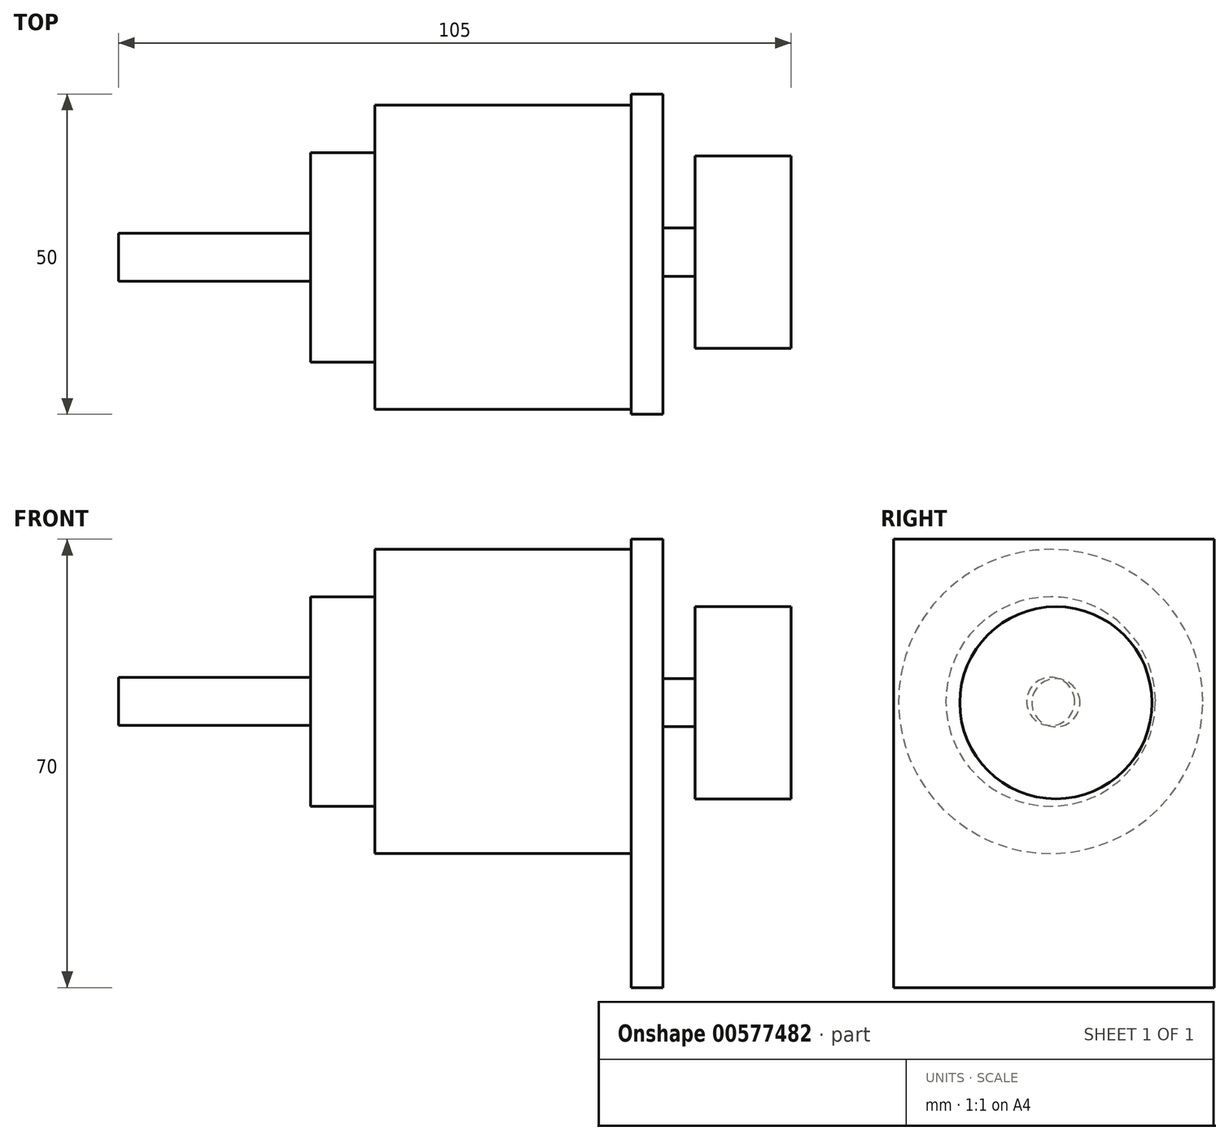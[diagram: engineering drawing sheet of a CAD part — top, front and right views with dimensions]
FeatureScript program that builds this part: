
annotation { "Feature Type Name" : "Feature", "Feature Type Description" : "" }
export const myFeature = defineFeature(function(context is Context, id is Id, definition is map)
    precondition{}
    {
        {
            var Q0;
            Q0=qCreatedBy(makeId("Front.planeOp"),FACE);
            var sketch = newSketch(context, id + "F0", { "sketchPlane" : qUnion([Q0])});
            skLineSegment(sketch, "E0.bottom", {"start": v(-2.5, 0.57) * mm, "end": v(2.5, 0.57) * mm});
            skLineSegment(sketch, "E0.top", {"start": v(-2.5, 70.57) * mm, "end": v(2.5, 70.57) * mm});
            skLineSegment(sketch, "E0.left", {"start": v(-2.5, 0.57) * mm, "end": v(-2.5, 70.57) * mm});
            skLineSegment(sketch, "E0.right", {"start": v(2.5, 0.57) * mm, "end": v(2.5, 70.57) * mm});
            skPoint(sketch, "E0.middle", {"position": v(0, 35.57) * mm});
            skSolve(sketch);
        }
        {
            var Q0;
            Q0=qSketchRegion(id+"F0",true);
            extrude(context, id + "F1", {"entities" : qUnion([Q0]), "oppositeDirection" : true, "depth" : 50 * mm});
        }
        {
            var Q0;
            Q0=makeQuery(id+"F1.opExtrude","SWEPT_FACE",FACE,{"disambiguationData":[OSD([sQuery(id+"F0.wireOp",EDGE,"E0.left")])]});
            var sketch = newSketch(context, id + "F2", { "sketchPlane" : qUnion([Q0])});
            skCircle(sketch, "E1", {"center": v(-24.5, 45.24) * mm, "radius": 23.75 * mm});
            skSolve(sketch);
        }
        {
            var Q0;
            Q0=qSketchRegion(id+"F2",true);
            extrude(context, id + "F3", {"entities" : qUnion([Q0]), "operationType" : NewBodyOperationType.ADD, "depth" : 40 * mm});
        }
        {
            var Q0;
            Q0=makeQuery(id+"F3.opExtrude","CAP_FACE",FACE,{"disambiguationData":[OSD([sQuery(id+"F2.wireOp",EDGE,"E1")])],"isStart":false});
            var sketch = newSketch(context, id + "F4", { "sketchPlane" : qUnion([Q0])});
            skCircle(sketch, "E2", {"center": v(-24.5, 45.24) * mm, "radius": 16.35 * mm});
            skSolve(sketch);
        }
        {
            var Q0;
            Q0=qSketchRegion(id+"F4",true);
            extrude(context, id + "F5", {"entities" : qUnion([Q0]), "operationType" : NewBodyOperationType.ADD, "depth" : 10 * mm});
        }
        {
            var Q0;
            Q0=makeQuery(id+"F5.opExtrude","CAP_FACE",FACE,{"disambiguationData":[OSD([sQuery(id+"F4.wireOp",EDGE,"E2")])],"isStart":false});
            var sketch = newSketch(context, id + "F6", { "sketchPlane" : qUnion([Q0])});
            skCircle(sketch, "E3", {"center": v(-24.5, 45.24) * mm, "radius": 3.75 * mm});
            skSolve(sketch);
        }
        {
            var Q0;
            Q0=qSketchRegion(id+"F6",true);
            extrude(context, id + "F7", {"entities" : qUnion([Q0]), "operationType" : NewBodyOperationType.ADD, "depth" : 30 * mm});
        }
        {
            var Q0;
            Q0=makeQuery(id+"F1.opExtrude","SWEPT_FACE",FACE,{"disambiguationData":[OSD([sQuery(id+"F0.wireOp",EDGE,"E0.right")])]});
            var sketch = newSketch(context, id + "F8", { "sketchPlane" : qUnion([Q0])});
            skCircle(sketch, "E4", {"center": v(25.32, 45.04) * mm, "radius": 3.75 * mm});
            skSolve(sketch);
        }
        {
            var Q0;
            Q0=qSketchRegion(id+"F8",true);
            extrude(context, id + "F9", {"entities" : qUnion([Q0]), "operationType" : NewBodyOperationType.ADD, "depth" : 5 * mm});
        }
        {
            var Q0;
            Q0=makeQuery(id+"F9.opExtrude","CAP_FACE",FACE,{"disambiguationData":[OSD([sQuery(id+"F8.wireOp",EDGE,"E4")])],"isStart":false});
            var sketch = newSketch(context, id + "F10", { "sketchPlane" : qUnion([Q0])});
            skCircle(sketch, "E5", {"center": v(25.32, 45.04) * mm, "radius": 15 * mm});
            skSolve(sketch);
        }
        {
            var Q0;
            Q0=qSketchRegion(id+"F10",true);
            extrude(context, id + "F11", {"entities" : qUnion([Q0]), "operationType" : NewBodyOperationType.ADD, "depth" : 15 * mm});
        }
    });
